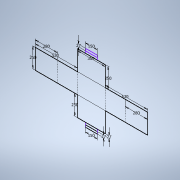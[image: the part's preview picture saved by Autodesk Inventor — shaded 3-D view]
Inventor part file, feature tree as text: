
AUTODESK INVENTOR PART (.ipt)
format: ipt  version: 2022 (Build 260153000, 153)  size: 107,008 bytes
history: native  units: mm
features: sketch x1
ambient origin geometry x8: Origin, YZ Plane, XZ Plane, XY Plane, X Axis, Y Axis, Z Axis, Center Point
feature tree (1):
  sketch  "Esboço1"  dims[d0=250.0mm d1=530.0mm d2=250.0mm d3=350.0mm d4=530.0mm d5=250.0mm d6=280.0mm d7=280.0mm d8=150.0mm d9=27.0mm d10=27.0mm d12=150.0mm d14=27.0mm]
